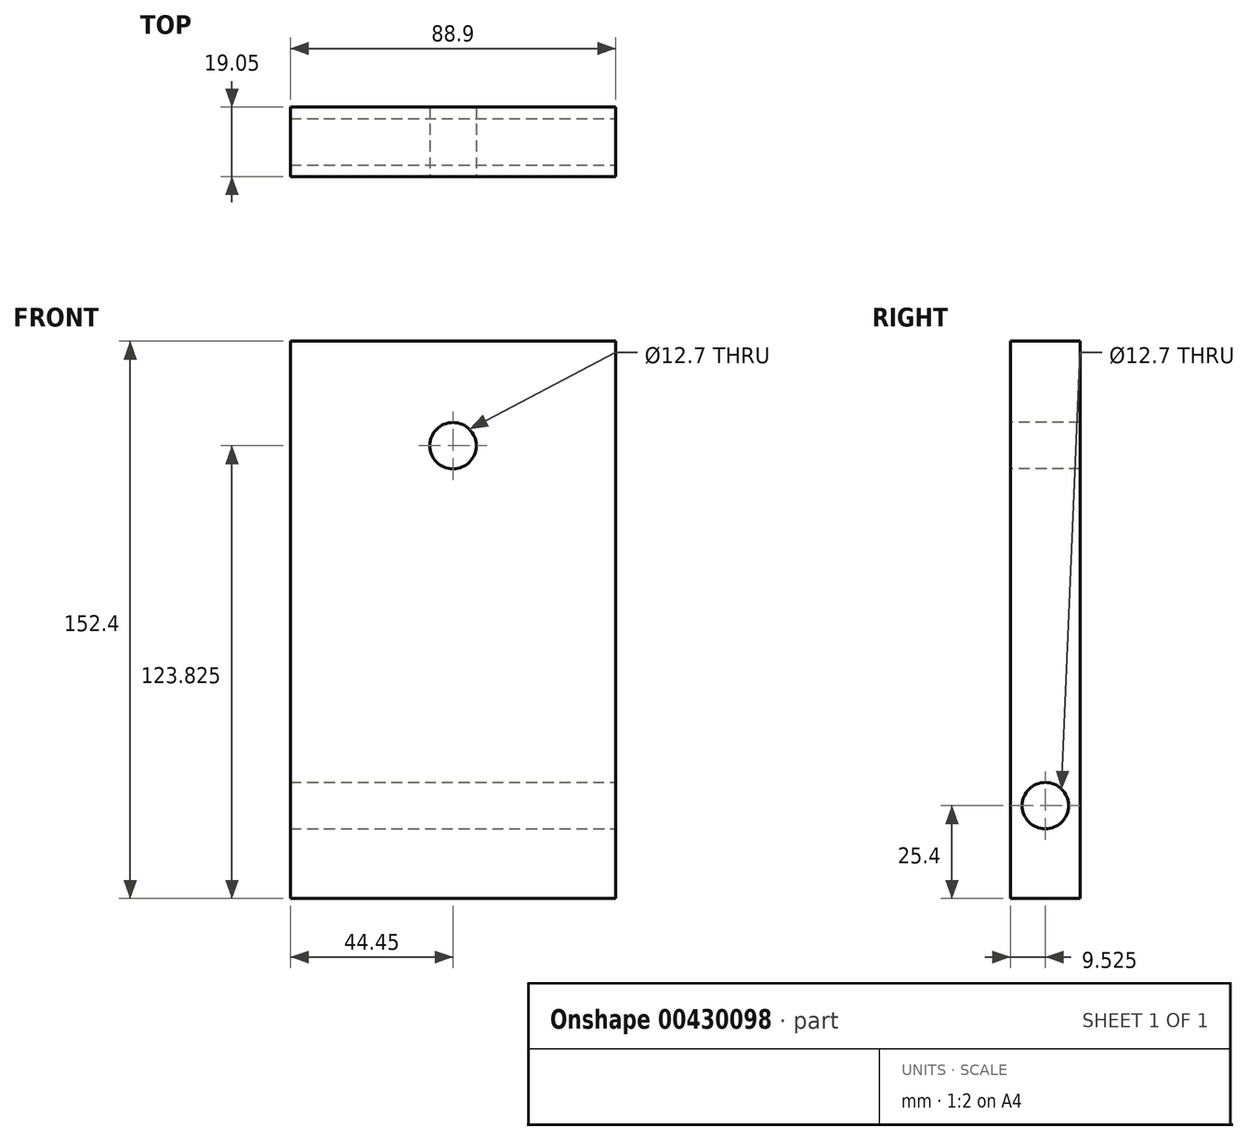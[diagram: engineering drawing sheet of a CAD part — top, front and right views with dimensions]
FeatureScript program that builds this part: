
annotation { "Feature Type Name" : "Feature", "Feature Type Description" : "" }
export const myFeature = defineFeature(function(context is Context, id is Id, definition is map)
    precondition{}
    {
        {
            var Q0;
            Q0=qCreatedBy(makeId("Top.planeOp"),FACE);
            var sketch = newSketch(context, id + "F0", { "sketchPlane" : qUnion([Q0])});
            skLineSegment(sketch, "E0.bottom", {"start": v(0, 0) * mm, "end": v(88.9, 0) * mm});
            skLineSegment(sketch, "E0.top", {"start": v(0, -19.05) * mm, "end": v(88.9, -19.05) * mm});
            skLineSegment(sketch, "E0.left", {"start": v(0, 0) * mm, "end": v(0, -19.05) * mm});
            skLineSegment(sketch, "E0.right", {"start": v(88.9, 0) * mm, "end": v(88.9, -19.05) * mm});
            skSolve(sketch);
        }
        {
            var Q0;
            Q0=makeQuery(id+"F0.imprint","IMPRINT",FACE,{"disambiguationData":[TD([[makeQuery(id+"F0.imprint","IMPRINT",EDGE,{"derivedFrom":sQuery(id+"F0.wireOp",EDGE,"E0.bottom")}),-1.0]])]});
            extrude(context, id + "F1", {"entities" : qUnion([Q0]), "depth" : 152.4 * mm});
        }
        {
            var Q0;
            Q0=makeQuery(id+"F1.opExtrude","SWEPT_FACE",FACE,{"disambiguationData":[OSD([sQuery(id+"F0.wireOp",EDGE,"E0.top")])]});
            var sketch = newSketch(context, id + "F2", { "sketchPlane" : qUnion([Q0])});
            skPoint(sketch, "E1", {"position": v(44.45, 123.83) * mm});
            skSolve(sketch);
        }
        {
            var Q0;
            Q0=sQuery(id+"F2.wireOp",VERTEX,"E1");
            var Q1;
            Q1=makeQuery(id+"F1.opExtrude","SWEPT_BODY",BODY,{"disambiguationData":[OSD([sQuery(id+"F0.wireOp",EDGE,"E0.bottom"),sQuery(id+"F0.wireOp",EDGE,"E0.top"),sQuery(id+"F0.wireOp",EDGE,"E0.left"),sQuery(id+"F0.wireOp",EDGE,"E0.right")])]});
            hole(context, id + "F3", {"style" : HoleStyle.SIMPLE, "endStyle" : HoleEndStyle.THROUGH, "holeDiameter" : 12.7 * mm, "isTappedThrough" : true, "tappedDepth" : 12.7 * mm, "tapClearance" : 3, "locations" : qUnion([Q0]), "scope" : qUnion([Q1])});
        }
        {
            var Q0;
            Q0=makeQuery(id+"F1.opExtrude","SWEPT_FACE",FACE,{"disambiguationData":[OSD([sQuery(id+"F0.wireOp",EDGE,"E0.right")])]});
            var sketch = newSketch(context, id + "F4", { "sketchPlane" : qUnion([Q0])});
            skPoint(sketch, "E2", {"position": v(-9.53, 25.4) * mm});
            skSolve(sketch);
        }
        {
            var Q0;
            Q0=sQuery(id+"F4.wireOp",VERTEX,"E2");
            var Q1;
            Q1=makeQuery(id+"F1.opExtrude","SWEPT_BODY",BODY,{"disambiguationData":[OSD([sQuery(id+"F0.wireOp",EDGE,"E0.bottom"),sQuery(id+"F0.wireOp",EDGE,"E0.top"),sQuery(id+"F0.wireOp",EDGE,"E0.left"),sQuery(id+"F0.wireOp",EDGE,"E0.right")])]});
            hole(context, id + "F5", {"style" : HoleStyle.SIMPLE, "endStyle" : HoleEndStyle.THROUGH, "holeDiameter" : 12.7 * mm, "isTappedThrough" : true, "tappedDepth" : 12.7 * mm, "tapClearance" : 3, "locations" : qUnion([Q0]), "scope" : qUnion([Q1])});
        }
    });
